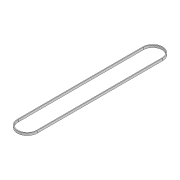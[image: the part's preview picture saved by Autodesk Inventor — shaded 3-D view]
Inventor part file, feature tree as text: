
AUTODESK INVENTOR PART (.ipt)
format: ipt  version: 2020 (Build 240168000, 168)  size: 87,040 bytes
history: native  units: mm
features: extrude x1, sketch x1
ambient origin geometry x8: Origin, YZ Plane, XZ Plane, XY Plane, X Axis, Y Axis, Z Axis, Center Point
bodies: Solid1 (feature_tree)
feature tree (2):
  extrude  "Extrusion1"  Depth=50.42mm
  sketch  "Sketch1"  dims[d0=343.0mm d1=50.42mm d2=50.42mm d3=2.0mm d4=2.0mm d5=6.0mm d6=0.0mm]
